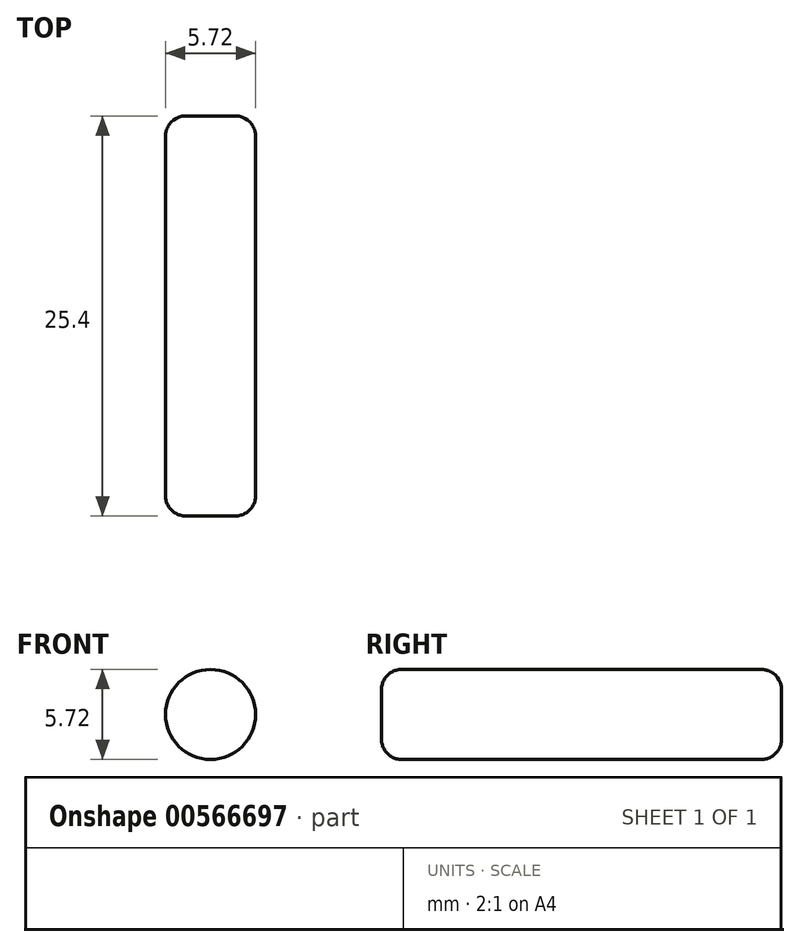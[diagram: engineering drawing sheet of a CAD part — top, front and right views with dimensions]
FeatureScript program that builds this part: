
annotation { "Feature Type Name" : "Feature", "Feature Type Description" : "" }
export const myFeature = defineFeature(function(context is Context, id is Id, definition is map)
    precondition{}
    {
        {
            var Q0;
            Q0=qCreatedBy(makeId("Front.planeOp"),FACE);
            var sketch = newSketch(context, id + "F0", { "sketchPlane" : qUnion([Q0])});
            skCircle(sketch, "E0", {"center": v(0, 0) * mm, "radius": 2.86 * mm});
            skSolve(sketch);
        }
        {
            var Q0;
            Q0 = qSketchRegion(id + "F0", true);
            extrude(context, id + "F1", {"entities" : qUnion([Q0]), "depth" : 25.4 * mm, "offsetDistance" : 25.4 * mm});
        }
        {
            var Q0;
            Q0=makeQuery(id+"F1.opExtrude","CAP_FACE",FACE,{"disambiguationData":[OSD([sQuery(id+"F0.wireOp",EDGE,"E0")])],"isStart":true});
            var Q1;
            Q1=makeQuery(id+"F1.opExtrude","CAP_FACE",FACE,{"disambiguationData":[OSD([sQuery(id+"F0.wireOp",EDGE,"E0")])],"isStart":false});
            fillet(context, id + "F2", {"entities" : qUnion([Q0, Q1]), "radius" : 1.27 * mm, "tangentPropagation" : true, "allowEdgeOverflow" : false});
        }
    });
